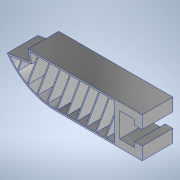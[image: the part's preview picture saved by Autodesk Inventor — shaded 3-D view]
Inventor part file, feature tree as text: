
AUTODESK INVENTOR PART (.ipt)
format: ipt  version: 2022 (Build 260153000, 153)  size: 289,792 bytes
history: native  units: mm
features: extrude x5, sketch x4, fillet x1, shell x1, projected_geometry x1
ambient origin geometry x8: Origin, YZ Plane, XZ Plane, XY Plane, X Axis, Y Axis, Z Axis, Center Point
bodies: Body1 (feature_tree)
feature tree (12):
  extrude  "Extrusion2"  Depth=5.8mm
  extrude  "Extrusion5"  Depth=12.0mm TaperAngle=0.0deg
  fillet  "Fillet2"  Radius=45.0mm
  shell  "Shell1"  Thickness=15.6mm
  extrude  "Extrusion7"  TaperAngle=0.0deg  [1 undecoded]
  extrude  "Extrusion8"  Depth=9.6mm
  extrude  "Extrusion9"  Depth=0.38mm
  sketch  "Sketch8"  dims[d41=5.8mm d48=44.0mm]
  sketch  "Sketch13"  dims[d50=3.0mm d56=12.0mm d57=0.0mm d63=45.0mm d67=15.6mm d71=0.0mm]
  sketch  "Sketch14"  dims[d80=17.453293mm d82=0.0mm d83=0.0mm]
  projected_geometry  "Projected Loop1"
  sketch  "Sketch15"  dims[d87=5.6mm d88=9.6mm d95=4.0mm d96=9.0mm d97=15.6mm d98=23.0mm d99=0.62mm d100=12.0mm d101=0.0mm d102=10.747401mm d103=12.0mm d104=0.0mm d105=0.38mm d1=0.38mm d127=12.0mm d128=0.0mm d129=3.81mm d130=19.198622mm d132=19.198622mm d133=0.38mm d135=0.38mm d136=0.38mm d137=0.38mm d138=0.38mm d139=0.38mm d140=0.38mm d141=0.38mm d142=3.81mm d143=0.38mm d144=3.81mm d145=3.81mm d146=3.81mm d147=3.81mm d148=3.81mm d149=3.81mm d150=3.81mm d151=3.81mm d152=19.198622mm]
note: 1 required parameter value undecoded (feature->parameter linkage not recoverable at this tier; creation-order binding heuristic only, values carry confidence <= 0.55)
